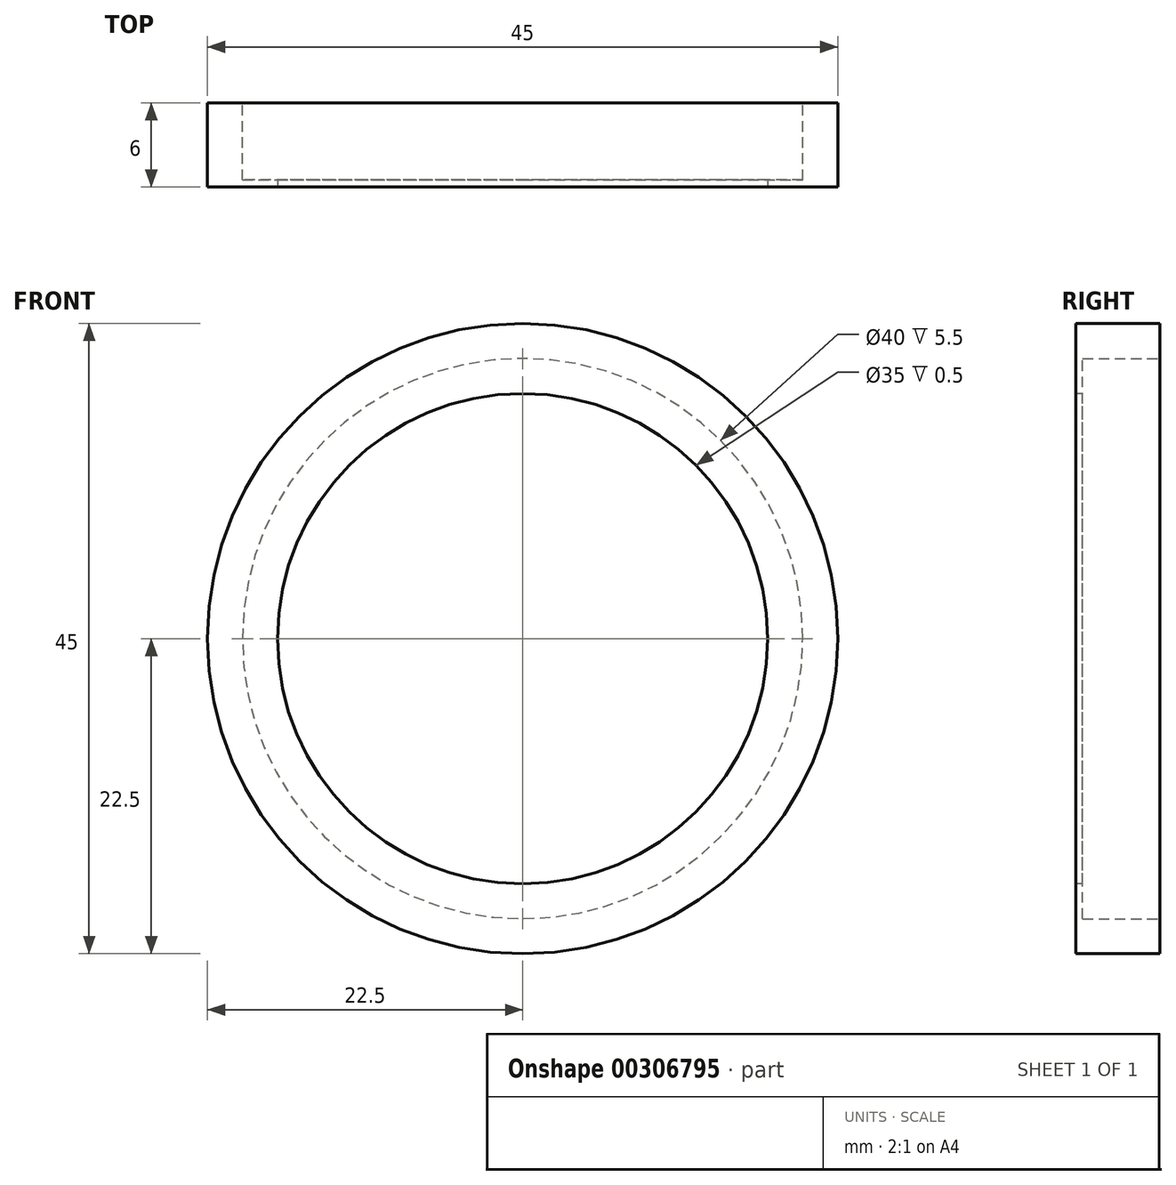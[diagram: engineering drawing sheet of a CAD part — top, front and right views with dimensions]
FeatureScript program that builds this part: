
annotation { "Feature Type Name" : "Feature", "Feature Type Description" : "" }
export const myFeature = defineFeature(function(context is Context, id is Id, definition is map)
    precondition{}
    {
        {
            var Q0;
            Q0=qCreatedBy(makeId("Front.planeOp"),FACE);
            var sketch = newSketch(context, id + "F0", { "sketchPlane" : qUnion([Q0])});
            skCircle(sketch, "E0", {"center": v(0, 0) * mm, "radius": 20 * mm});
            skCircle(sketch, "E1", {"center": v(0, 0) * mm, "radius": 22.5 * mm});
            skSolve(sketch);
        }
        {
            var Q0;
            Q0=makeQuery(id+"F0.imprint","IMPRINT",FACE,{"disambiguationData":[TD([[makeQuery(id+"F0.imprint","IMPRINT",EDGE,{"derivedFrom":sQuery(id+"F0.wireOp",EDGE,"E0")}),-1.0]])]});
            extrude(context, id + "F1", {"entities" : qUnion([Q0]), "endBound" : BoundingType.SYMMETRIC, "depth" : 6 * mm});
        }
        {
            var Q0;
            Q0=makeQuery(id+"F1.opExtrude","CAP_FACE",FACE,{"disambiguationData":[OSD([sQuery(id+"F0.wireOp",EDGE,"E0"),sQuery(id+"F0.wireOp",EDGE,"E1")])],"isStart":false});
            var sketch = newSketch(context, id + "F2", { "sketchPlane" : qUnion([Q0])});
            skCircle(sketch, "E2", {"center": v(0, 0) * mm, "radius": 20 * mm});
            skCircle(sketch, "E3", {"center": v(0, 0) * mm, "radius": 17.5 * mm});
            skSolve(sketch);
        }
        {
            var Q0;
            Q0=makeQuery(id+"F2.imprint","IMPRINT",FACE,{"disambiguationData":[TD([[makeQuery(id+"F2.imprint","IMPRINT",EDGE,{"derivedFrom":sQuery(id+"F2.wireOp",EDGE,"E2")}),1.0]])]});
            extrude(context, id + "F3", {"entities" : qUnion([Q0]), "operationType" : NewBodyOperationType.ADD, "oppositeDirection" : true, "depth" : 0.5 * mm});
        }
    });
